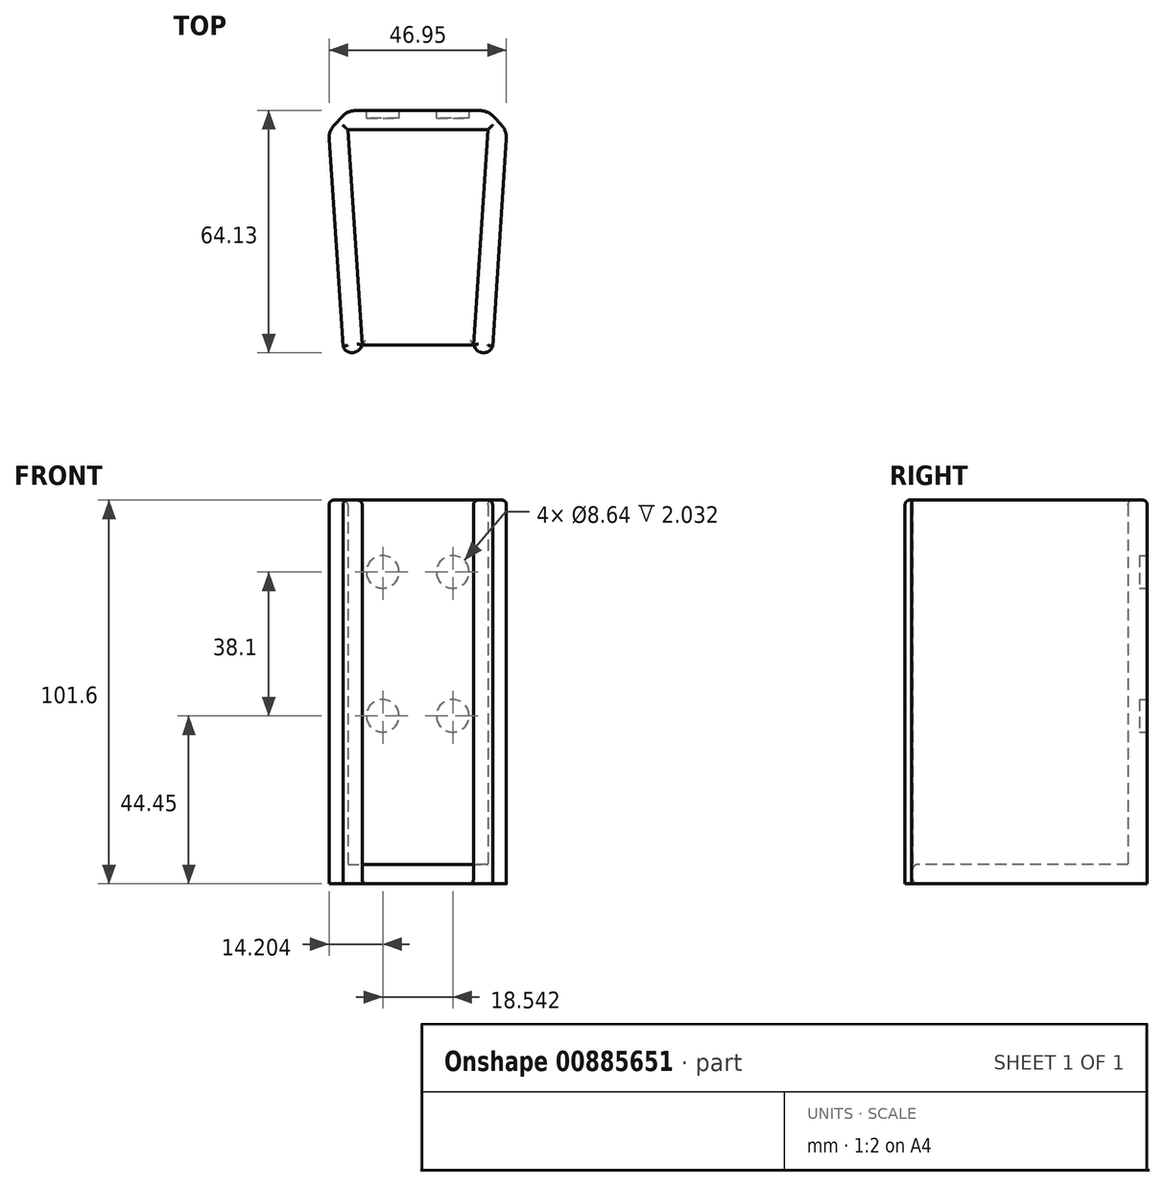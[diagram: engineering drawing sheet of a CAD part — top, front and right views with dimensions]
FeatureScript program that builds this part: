
annotation { "Feature Type Name" : "Feature", "Feature Type Description" : "" }
export const myFeature = defineFeature(function(context is Context, id is Id, definition is map)
    precondition{}
    {
        {
            var Q0;
            Q0=qCreatedBy(makeId("Top.planeOp"),FACE);
            var sketch = newSketch(context, id + "F0", { "sketchPlane" : qUnion([Q0])});
            skLineSegment(sketch, "E0", {"start": v(-16.69, 57.02) * mm, "end": v(20.4, 57.02) * mm});
            skLineSegment(sketch, "E1", {"start": v(-12.88, 0) * mm, "end": v(16.59, 0) * mm});
            skLineSegment(sketch, "E2", {"start": v(-16.69, 57.02) * mm, "end": v(-12.88, 0) * mm});
            skLineSegment(sketch, "E3", {"start": v(20.4, 57.02) * mm, "end": v(16.59, 0) * mm});
            skPoint(sketch, "E4", {"position": v(1.86, 57.02) * mm});
            skPoint(sketch, "E5", {"position": v(1.86, 0) * mm});
            skLineSegment(sketch, "E6.0", {"start": v(-16.69, 62.1) * mm, "end": v(20.4, 62.1) * mm});
            skLineSegment(sketch, "E7", {"start": v(20.4, 62.1) * mm, "end": v(20.4, 57.02) * mm});
            skLineSegment(sketch, "E8", {"start": v(-16.69, 62.1) * mm, "end": v(-16.69, 57.02) * mm});
            skLineSegment(sketch, "E9.0", {"start": v(-21.76, 56.68) * mm, "end": v(-17.95, -0.34) * mm});
            skLineSegment(sketch, "E10.0", {"start": v(25.47, 56.68) * mm, "end": v(21.66, -0.34) * mm});
            skLineSegment(sketch, "E11", {"start": v(-21.76, 56.68) * mm, "end": v(-16.69, 62.1) * mm});
            skLineSegment(sketch, "E12", {"start": v(20.4, 62.1) * mm, "end": v(25.47, 56.68) * mm});
            skLineSegment(sketch, "E13", {"start": v(21.66, -0.34) * mm, "end": v(20.4, -6.12) * mm});
            skLineSegment(sketch, "E14", {"start": v(16.59, 0) * mm, "end": v(20.4, -6.12) * mm});
            skLineSegment(sketch, "E15", {"start": v(1.86, 57.02) * mm, "end": v(1.86, 0) * mm, "construction": true});
            skLineSegment(sketch, "E16.MirrorCS", {"start": v(-12.88, 0) * mm, "end": v(-16.69, -6.12) * mm});
            skLineSegment(sketch, "E17.MirrorCS", {"start": v(-17.95, -0.34) * mm, "end": v(-16.69, -6.12) * mm});
            skSolve(sketch);
        }
        {
            var Q0;
            Q0=makeQuery(id+"F0.imprint","IMPRINT",FACE,{"disambiguationData":[TD([[makeQuery(id+"F0.imprint","IMPRINT",EDGE,{"derivedFrom":sQuery(id+"F0.wireOp",EDGE,"E2")}),-1.0]])]});
            var Q1;
            Q1=makeQuery(id+"F0.imprint","IMPRINT",FACE,{"disambiguationData":[TD([[makeQuery(id+"F0.imprint","IMPRINT",EDGE,{"derivedFrom":sQuery(id+"F0.wireOp",EDGE,"E0")}),1.0]])]});
            var Q2;
            Q2=makeQuery(id+"F0.imprint","IMPRINT",FACE,{"disambiguationData":[TD([[makeQuery(id+"F0.imprint","IMPRINT",EDGE,{"derivedFrom":sQuery(id+"F0.wireOp",EDGE,"E3")}),1.0]])]});
            extrude(context, id + "F1", {"entities" : qUnion([Q0, Q1, Q2]), "depth" : 96.52 * mm, "offsetDistance" : 25.4 * mm});
        }
        {
            var Q0;
            Q0=makeQuery(id+"F0.imprint","IMPRINT",FACE,{"disambiguationData":[TD([[makeQuery(id+"F0.imprint","IMPRINT",EDGE,{"derivedFrom":sQuery(id+"F0.wireOp",EDGE,"E0")}),-1.0]])]});
            var Q1;
            Q1=makeQuery(id+"F0.imprint","IMPRINT",FACE,{"disambiguationData":[TD([[makeQuery(id+"F0.imprint","IMPRINT",EDGE,{"derivedFrom":sQuery(id+"F0.wireOp",EDGE,"E3")}),1.0]])]});
            var Q2;
            Q2=makeQuery(id+"F0.imprint","IMPRINT",FACE,{"disambiguationData":[TD([[makeQuery(id+"F0.imprint","IMPRINT",EDGE,{"derivedFrom":sQuery(id+"F0.wireOp",EDGE,"E0")}),1.0]])]});
            var Q3;
            Q3=makeQuery(id+"F0.imprint","IMPRINT",FACE,{"disambiguationData":[TD([[makeQuery(id+"F0.imprint","IMPRINT",EDGE,{"derivedFrom":sQuery(id+"F0.wireOp",EDGE,"E2")}),-1.0]])]});
            extrude(context, id + "F2", {"entities" : qUnion([Q0, Q1, Q2, Q3]), "operationType" : NewBodyOperationType.ADD, "oppositeDirection" : true, "depth" : 5.08 * mm, "offsetDistance" : 25.4 * mm});
        }
        {
            var Q0;
            {var subQ0=sQuery(id+"F0.wireOp",EDGE,"E6.0");Q0=makeQuery(id+"F2.boolean.opBoolean","MERGE",FACE,{"derivedFrom":[makeQuery(id+"F1.opExtrude","SWEPT_FACE",FACE,{"disambiguationData":[OSD([subQ0])]}),makeQuery(id+"F2.opExtrude","SWEPT_FACE",FACE,{"disambiguationData":[OSD([subQ0])]})]});}
            var sketch = newSketch(context, id + "F3", { "sketchPlane" : qUnion([Q0])});
            skLineSegment(sketch, "E18", {"start": v(-1.86, 96.52) * mm, "end": v(-1.86, 0) * mm, "construction": true});
            skPoint(sketch, "E19", {"position": v(-1.86, 20.32) * mm});
            skPoint(sketch, "E20", {"position": v(-1.86, 77.47) * mm});
            skPoint(sketch, "E21", {"position": v(-1.86, 39.37) * mm});
            skPoint(sketch, "E22", {"position": v(-20.4, 39.37) * mm});
            skPoint(sketch, "E23", {"position": v(-20.4, 77.47) * mm});
            skPoint(sketch, "E24", {"position": v(16.69, 77.47) * mm});
            skPoint(sketch, "E25", {"position": v(16.69, 39.37) * mm});
            skLineSegment(sketch, "E26", {"start": v(-20.4, 77.47) * mm, "end": v(-1.86, 77.47) * mm, "construction": true});
            skLineSegment(sketch, "E27", {"start": v(-1.86, 77.47) * mm, "end": v(16.69, 77.47) * mm, "construction": true});
            skLineSegment(sketch, "E28", {"start": v(16.69, 39.37) * mm, "end": v(-1.86, 39.37) * mm, "construction": true});
            skLineSegment(sketch, "E29", {"start": v(-1.86, 39.37) * mm, "end": v(-20.4, 39.37) * mm, "construction": true});
            skCircle(sketch, "E30", {"center": v(-11.13, 77.47) * mm, "radius": 4.32 * mm});
            skCircle(sketch, "E31", {"center": v(7.42, 77.47) * mm, "radius": 4.32 * mm});
            skCircle(sketch, "E32", {"center": v(7.42, 39.37) * mm, "radius": 4.32 * mm});
            skCircle(sketch, "E33", {"center": v(-11.13, 39.37) * mm, "radius": 4.32 * mm});
            skSolve(sketch);
        }
        {
            var Q0;
            {var subQ0=sQuery(id+"F0.wireOp",EDGE,"E17.MirrorCS");var subQ1=sQuery(id+"F0.wireOp",EDGE,"E16.MirrorCS");Q0=makeQuery(id+"F2.boolean.opBoolean","MERGE",EDGE,{"derivedFrom":[makeQuery(id+"F1.opExtrude","SWEPT_EDGE",EDGE,{"disambiguationData":[OSD([subQ1,subQ0])]}),makeQuery(id+"F2.opExtrude","SWEPT_EDGE",EDGE,{"disambiguationData":[OSD([subQ1,subQ0])]})]});}
            var Q1;
            {var subQ0=sQuery(id+"F0.wireOp",EDGE,"E14");var subQ1=sQuery(id+"F0.wireOp",EDGE,"E13");Q1=makeQuery(id+"F2.boolean.opBoolean","MERGE",EDGE,{"derivedFrom":[makeQuery(id+"F1.opExtrude","SWEPT_EDGE",EDGE,{"disambiguationData":[OSD([subQ1,subQ0])]}),makeQuery(id+"F2.opExtrude","SWEPT_EDGE",EDGE,{"disambiguationData":[OSD([subQ1,subQ0])]})]});}
            fillet(context, id + "F4", {"entities" : qUnion([Q0, Q1]), "radius" : 2.54 * mm, "tangentPropagation" : true, "allowEdgeOverflow" : false});
        }
        {
            var Q0;
            {var subQ0=sQuery(id+"F0.wireOp",EDGE,"E11");var subQ1=sQuery(id+"F0.wireOp",EDGE,"E9.0");Q0=makeQuery(id+"F2.boolean.opBoolean","MERGE",EDGE,{"derivedFrom":[makeQuery(id+"F1.opExtrude","SWEPT_EDGE",EDGE,{"disambiguationData":[OSD([subQ1,subQ0])]}),makeQuery(id+"F2.opExtrude","SWEPT_EDGE",EDGE,{"disambiguationData":[OSD([subQ1,subQ0])]})]});}
            var Q1;
            {var subQ0=sQuery(id+"F0.wireOp",EDGE,"E11");var subQ1=sQuery(id+"F0.wireOp",EDGE,"E8");var subQ2=sQuery(id+"F0.wireOp",EDGE,"E6.0");Q1=makeQuery(id+"F2.boolean.opBoolean","MERGE",EDGE,{"derivedFrom":[makeQuery(id+"F1.opExtrude","SWEPT_EDGE",EDGE,{"disambiguationData":[OSD([subQ2,subQ1,subQ0])]}),makeQuery(id+"F2.opExtrude","SWEPT_EDGE",EDGE,{"disambiguationData":[OSD([subQ2,subQ1,subQ0])]})]});}
            var Q2;
            {var subQ0=sQuery(id+"F0.wireOp",EDGE,"E12");var subQ1=sQuery(id+"F0.wireOp",EDGE,"E7");var subQ2=sQuery(id+"F0.wireOp",EDGE,"E6.0");Q2=makeQuery(id+"F2.boolean.opBoolean","MERGE",EDGE,{"derivedFrom":[makeQuery(id+"F1.opExtrude","SWEPT_EDGE",EDGE,{"disambiguationData":[OSD([subQ2,subQ1,subQ0])]}),makeQuery(id+"F2.opExtrude","SWEPT_EDGE",EDGE,{"disambiguationData":[OSD([subQ2,subQ1,subQ0])]})]});}
            var Q3;
            {var subQ0=sQuery(id+"F0.wireOp",EDGE,"E12");var subQ1=sQuery(id+"F0.wireOp",EDGE,"E10.0");Q3=makeQuery(id+"F2.boolean.opBoolean","MERGE",EDGE,{"derivedFrom":[makeQuery(id+"F1.opExtrude","SWEPT_EDGE",EDGE,{"disambiguationData":[OSD([subQ1,subQ0])]}),makeQuery(id+"F2.opExtrude","SWEPT_EDGE",EDGE,{"disambiguationData":[OSD([subQ1,subQ0])]})]});}
            fillet(context, id + "F5", {"entities" : qUnion([Q0, Q1, Q2, Q3]), "radius" : 5.08 * mm, "tangentPropagation" : true, "allowEdgeOverflow" : false});
        }
        {
            var Q0;
            Q0=makeQuery(id+"F3.imprint","IMPRINT",FACE,{"disambiguationData":[TD([[makeQuery(id+"F3.imprint","IMPRINT",EDGE,{"derivedFrom":sQuery(id+"F3.wireOp",EDGE,"E30")}),1.0]])]});
            var Q1;
            Q1=makeQuery(id+"F3.imprint","IMPRINT",FACE,{"disambiguationData":[TD([[makeQuery(id+"F3.imprint","IMPRINT",EDGE,{"derivedFrom":sQuery(id+"F3.wireOp",EDGE,"E31")}),1.0]])]});
            var Q2;
            Q2=makeQuery(id+"F3.imprint","IMPRINT",FACE,{"disambiguationData":[TD([[makeQuery(id+"F3.imprint","IMPRINT",EDGE,{"derivedFrom":sQuery(id+"F3.wireOp",EDGE,"E32")}),1.0]])]});
            var Q3;
            Q3=makeQuery(id+"F3.imprint","IMPRINT",FACE,{"disambiguationData":[TD([[makeQuery(id+"F3.imprint","IMPRINT",EDGE,{"derivedFrom":sQuery(id+"F3.wireOp",EDGE,"E33")}),1.0]])]});
            extrude(context, id + "F6", {"entities" : qUnion([Q0, Q1, Q2, Q3]), "operationType" : NewBodyOperationType.REMOVE, "oppositeDirection" : true, "depth" : 2.03 * mm, "offsetDistance" : 25.4 * mm});
        }
        {
            var Q0;
            Q0=makeQuery(id+"F1.opExtrude","CAP_EDGE",EDGE,{"disambiguationData":[OSD([sQuery(id+"F0.wireOp",EDGE,"E0")])],"isStart":true});
            var Q1;
            Q1=makeQuery(id+"F1.opExtrude","CAP_EDGE",EDGE,{"disambiguationData":[OSD([sQuery(id+"F0.wireOp",EDGE,"E3")])],"isStart":true});
            var Q2;
            Q2=makeQuery(id+"F1.opExtrude","CAP_EDGE",EDGE,{"disambiguationData":[OSD([sQuery(id+"F0.wireOp",EDGE,"E2")])],"isStart":true});
            var Q3;
            Q3=makeQuery(id+"F1.opExtrude","CAP_EDGE",EDGE,{"disambiguationData":[OSD([sQuery(id+"F0.wireOp",EDGE,"E2")])],"isStart":false});
            var Q4;
            Q4=makeQuery(id+"F1.opExtrude","CAP_EDGE",EDGE,{"disambiguationData":[OSD([sQuery(id+"F0.wireOp",EDGE,"E3")])],"isStart":false});
            var Q5;
            Q5=makeQuery(id+"F1.opExtrude","CAP_EDGE",EDGE,{"disambiguationData":[OSD([sQuery(id+"F0.wireOp",EDGE,"E10.0")])],"isStart":false});
            var Q6;
            Q6=makeQuery(id+"F1.opExtrude","CAP_EDGE",EDGE,{"disambiguationData":[OSD([sQuery(id+"F0.wireOp",EDGE,"E9.0")])],"isStart":false});
            var Q7;
            Q7=makeQuery(id+"F1.opExtrude","CAP_EDGE",EDGE,{"disambiguationData":[OSD([sQuery(id+"F0.wireOp",EDGE,"E6.0")])],"isStart":false});
            var Q8;
            Q8=makeQuery(id+"F1.opExtrude","CAP_EDGE",EDGE,{"disambiguationData":[OSD([sQuery(id+"F0.wireOp",EDGE,"E12")])],"isStart":false});
            var Q9;
            {var subQ0=sQuery(id+"F0.wireOp",EDGE,"E12");var subQ1=sQuery(id+"F0.wireOp",EDGE,"E6.0");var subQ2=sQuery(id+"F0.wireOp",EDGE,"E7");Q9=makeQuery(id+"F5.opFillet","BLEND_EDGE",EDGE,{"blendedFrom":[makeQuery(id+"F2.boolean.opBoolean","MERGE",EDGE,{"derivedFrom":[makeQuery(id+"F1.opExtrude","SWEPT_EDGE",EDGE,{"disambiguationData":[OSD([subQ1,subQ2,subQ0])]}),makeQuery(id+"F2.opExtrude","SWEPT_EDGE",EDGE,{"disambiguationData":[OSD([subQ1,subQ2,subQ0])]})]}),makeQuery(id+"F1.opExtrude","CAP_FACE",FACE,{"disambiguationData":[OSD([sQuery(id+"F0.wireOp",EDGE,"E0"),sQuery(id+"F0.wireOp",EDGE,"E2"),sQuery(id+"F0.wireOp",EDGE,"E3"),subQ1,sQuery(id+"F0.wireOp",EDGE,"E9.0"),sQuery(id+"F0.wireOp",EDGE,"E10.0"),sQuery(id+"F0.wireOp",EDGE,"E11"),subQ0,sQuery(id+"F0.wireOp",EDGE,"E13"),sQuery(id+"F0.wireOp",EDGE,"E14"),sQuery(id+"F0.wireOp",EDGE,"E16.MirrorCS"),sQuery(id+"F0.wireOp",EDGE,"E17.MirrorCS")])],"isStart":false})],"blendedInto":[makeQuery(id+"F1.opExtrude","CAP_FACE",FACE,{"disambiguationData":[OSD([sQuery(id+"F0.wireOp",EDGE,"E0"),sQuery(id+"F0.wireOp",EDGE,"E2"),sQuery(id+"F0.wireOp",EDGE,"E3"),subQ1,sQuery(id+"F0.wireOp",EDGE,"E9.0"),sQuery(id+"F0.wireOp",EDGE,"E10.0"),sQuery(id+"F0.wireOp",EDGE,"E11"),subQ0,sQuery(id+"F0.wireOp",EDGE,"E13"),sQuery(id+"F0.wireOp",EDGE,"E14"),sQuery(id+"F0.wireOp",EDGE,"E16.MirrorCS"),sQuery(id+"F0.wireOp",EDGE,"E17.MirrorCS")])],"isStart":false})]});}
            var Q10;
            {var subQ0=sQuery(id+"F0.wireOp",EDGE,"E12");var subQ1=sQuery(id+"F0.wireOp",EDGE,"E10.0");Q10=makeQuery(id+"F5.opFillet","BLEND_EDGE",EDGE,{"blendedFrom":[makeQuery(id+"F2.boolean.opBoolean","MERGE",EDGE,{"derivedFrom":[makeQuery(id+"F1.opExtrude","SWEPT_EDGE",EDGE,{"disambiguationData":[OSD([subQ1,subQ0])]}),makeQuery(id+"F2.opExtrude","SWEPT_EDGE",EDGE,{"disambiguationData":[OSD([subQ1,subQ0])]})]}),makeQuery(id+"F1.opExtrude","CAP_FACE",FACE,{"disambiguationData":[OSD([sQuery(id+"F0.wireOp",EDGE,"E0"),sQuery(id+"F0.wireOp",EDGE,"E2"),sQuery(id+"F0.wireOp",EDGE,"E3"),sQuery(id+"F0.wireOp",EDGE,"E6.0"),sQuery(id+"F0.wireOp",EDGE,"E9.0"),subQ1,sQuery(id+"F0.wireOp",EDGE,"E11"),subQ0,sQuery(id+"F0.wireOp",EDGE,"E13"),sQuery(id+"F0.wireOp",EDGE,"E14"),sQuery(id+"F0.wireOp",EDGE,"E16.MirrorCS"),sQuery(id+"F0.wireOp",EDGE,"E17.MirrorCS")])],"isStart":false})],"blendedInto":[makeQuery(id+"F1.opExtrude","CAP_FACE",FACE,{"disambiguationData":[OSD([sQuery(id+"F0.wireOp",EDGE,"E0"),sQuery(id+"F0.wireOp",EDGE,"E2"),sQuery(id+"F0.wireOp",EDGE,"E3"),sQuery(id+"F0.wireOp",EDGE,"E6.0"),sQuery(id+"F0.wireOp",EDGE,"E9.0"),subQ1,sQuery(id+"F0.wireOp",EDGE,"E11"),subQ0,sQuery(id+"F0.wireOp",EDGE,"E13"),sQuery(id+"F0.wireOp",EDGE,"E14"),sQuery(id+"F0.wireOp",EDGE,"E16.MirrorCS"),sQuery(id+"F0.wireOp",EDGE,"E17.MirrorCS")])],"isStart":false})]});}
            var Q11;
            {var subQ0=sQuery(id+"F0.wireOp",EDGE,"E11");var subQ1=sQuery(id+"F0.wireOp",EDGE,"E6.0");var subQ2=sQuery(id+"F0.wireOp",EDGE,"E8");Q11=makeQuery(id+"F5.opFillet","BLEND_EDGE",EDGE,{"blendedFrom":[makeQuery(id+"F2.boolean.opBoolean","MERGE",EDGE,{"derivedFrom":[makeQuery(id+"F1.opExtrude","SWEPT_EDGE",EDGE,{"disambiguationData":[OSD([subQ1,subQ2,subQ0])]}),makeQuery(id+"F2.opExtrude","SWEPT_EDGE",EDGE,{"disambiguationData":[OSD([subQ1,subQ2,subQ0])]})]}),makeQuery(id+"F1.opExtrude","CAP_FACE",FACE,{"disambiguationData":[OSD([sQuery(id+"F0.wireOp",EDGE,"E0"),sQuery(id+"F0.wireOp",EDGE,"E2"),sQuery(id+"F0.wireOp",EDGE,"E3"),subQ1,sQuery(id+"F0.wireOp",EDGE,"E9.0"),sQuery(id+"F0.wireOp",EDGE,"E10.0"),subQ0,sQuery(id+"F0.wireOp",EDGE,"E12"),sQuery(id+"F0.wireOp",EDGE,"E13"),sQuery(id+"F0.wireOp",EDGE,"E14"),sQuery(id+"F0.wireOp",EDGE,"E16.MirrorCS"),sQuery(id+"F0.wireOp",EDGE,"E17.MirrorCS")])],"isStart":false})],"blendedInto":[makeQuery(id+"F1.opExtrude","CAP_FACE",FACE,{"disambiguationData":[OSD([sQuery(id+"F0.wireOp",EDGE,"E0"),sQuery(id+"F0.wireOp",EDGE,"E2"),sQuery(id+"F0.wireOp",EDGE,"E3"),subQ1,sQuery(id+"F0.wireOp",EDGE,"E9.0"),sQuery(id+"F0.wireOp",EDGE,"E10.0"),subQ0,sQuery(id+"F0.wireOp",EDGE,"E12"),sQuery(id+"F0.wireOp",EDGE,"E13"),sQuery(id+"F0.wireOp",EDGE,"E14"),sQuery(id+"F0.wireOp",EDGE,"E16.MirrorCS"),sQuery(id+"F0.wireOp",EDGE,"E17.MirrorCS")])],"isStart":false})]});}
            var Q12;
            Q12=makeQuery(id+"F1.opExtrude","CAP_EDGE",EDGE,{"disambiguationData":[OSD([sQuery(id+"F0.wireOp",EDGE,"E11")])],"isStart":false});
            var Q13;
            {var subQ0=sQuery(id+"F0.wireOp",EDGE,"E11");var subQ1=sQuery(id+"F0.wireOp",EDGE,"E9.0");Q13=makeQuery(id+"F5.opFillet","BLEND_EDGE",EDGE,{"blendedFrom":[makeQuery(id+"F2.boolean.opBoolean","MERGE",EDGE,{"derivedFrom":[makeQuery(id+"F1.opExtrude","SWEPT_EDGE",EDGE,{"disambiguationData":[OSD([subQ1,subQ0])]}),makeQuery(id+"F2.opExtrude","SWEPT_EDGE",EDGE,{"disambiguationData":[OSD([subQ1,subQ0])]})]}),makeQuery(id+"F1.opExtrude","CAP_FACE",FACE,{"disambiguationData":[OSD([sQuery(id+"F0.wireOp",EDGE,"E0"),sQuery(id+"F0.wireOp",EDGE,"E2"),sQuery(id+"F0.wireOp",EDGE,"E3"),sQuery(id+"F0.wireOp",EDGE,"E6.0"),subQ1,sQuery(id+"F0.wireOp",EDGE,"E10.0"),subQ0,sQuery(id+"F0.wireOp",EDGE,"E12"),sQuery(id+"F0.wireOp",EDGE,"E13"),sQuery(id+"F0.wireOp",EDGE,"E14"),sQuery(id+"F0.wireOp",EDGE,"E16.MirrorCS"),sQuery(id+"F0.wireOp",EDGE,"E17.MirrorCS")])],"isStart":false})],"blendedInto":[makeQuery(id+"F1.opExtrude","CAP_FACE",FACE,{"disambiguationData":[OSD([sQuery(id+"F0.wireOp",EDGE,"E0"),sQuery(id+"F0.wireOp",EDGE,"E2"),sQuery(id+"F0.wireOp",EDGE,"E3"),sQuery(id+"F0.wireOp",EDGE,"E6.0"),subQ1,sQuery(id+"F0.wireOp",EDGE,"E10.0"),subQ0,sQuery(id+"F0.wireOp",EDGE,"E12"),sQuery(id+"F0.wireOp",EDGE,"E13"),sQuery(id+"F0.wireOp",EDGE,"E14"),sQuery(id+"F0.wireOp",EDGE,"E16.MirrorCS"),sQuery(id+"F0.wireOp",EDGE,"E17.MirrorCS")])],"isStart":false})]});}
            var Q14;
            Q14=makeQuery(id+"F1.opExtrude","CAP_EDGE",EDGE,{"disambiguationData":[OSD([sQuery(id+"F0.wireOp",EDGE,"E0")])],"isStart":false});
            var Q15;
            {var subQ0=sQuery(id+"F0.wireOp",EDGE,"E14");var subQ1=sQuery(id+"F0.wireOp",EDGE,"E13");Q15=makeQuery(id+"F4.opFillet","BLEND_EDGE",EDGE,{"blendedFrom":[makeQuery(id+"F2.boolean.opBoolean","MERGE",EDGE,{"derivedFrom":[makeQuery(id+"F1.opExtrude","SWEPT_EDGE",EDGE,{"disambiguationData":[OSD([subQ1,subQ0])]}),makeQuery(id+"F2.opExtrude","SWEPT_EDGE",EDGE,{"disambiguationData":[OSD([subQ1,subQ0])]})]}),makeQuery(id+"F1.opExtrude","CAP_FACE",FACE,{"disambiguationData":[OSD([sQuery(id+"F0.wireOp",EDGE,"E0"),sQuery(id+"F0.wireOp",EDGE,"E2"),sQuery(id+"F0.wireOp",EDGE,"E3"),sQuery(id+"F0.wireOp",EDGE,"E6.0"),sQuery(id+"F0.wireOp",EDGE,"E9.0"),sQuery(id+"F0.wireOp",EDGE,"E10.0"),sQuery(id+"F0.wireOp",EDGE,"E11"),sQuery(id+"F0.wireOp",EDGE,"E12"),subQ1,subQ0,sQuery(id+"F0.wireOp",EDGE,"E16.MirrorCS"),sQuery(id+"F0.wireOp",EDGE,"E17.MirrorCS")])],"isStart":false})],"blendedInto":[makeQuery(id+"F1.opExtrude","CAP_FACE",FACE,{"disambiguationData":[OSD([sQuery(id+"F0.wireOp",EDGE,"E0"),sQuery(id+"F0.wireOp",EDGE,"E2"),sQuery(id+"F0.wireOp",EDGE,"E3"),sQuery(id+"F0.wireOp",EDGE,"E6.0"),sQuery(id+"F0.wireOp",EDGE,"E9.0"),sQuery(id+"F0.wireOp",EDGE,"E10.0"),sQuery(id+"F0.wireOp",EDGE,"E11"),sQuery(id+"F0.wireOp",EDGE,"E12"),subQ1,subQ0,sQuery(id+"F0.wireOp",EDGE,"E16.MirrorCS"),sQuery(id+"F0.wireOp",EDGE,"E17.MirrorCS")])],"isStart":false})]});}
            var Q16;
            {var subQ0=sQuery(id+"F0.wireOp",EDGE,"E17.MirrorCS");var subQ1=sQuery(id+"F0.wireOp",EDGE,"E16.MirrorCS");Q16=makeQuery(id+"F4.opFillet","BLEND_EDGE",EDGE,{"blendedFrom":[makeQuery(id+"F2.boolean.opBoolean","MERGE",EDGE,{"derivedFrom":[makeQuery(id+"F1.opExtrude","SWEPT_EDGE",EDGE,{"disambiguationData":[OSD([subQ1,subQ0])]}),makeQuery(id+"F2.opExtrude","SWEPT_EDGE",EDGE,{"disambiguationData":[OSD([subQ1,subQ0])]})]}),makeQuery(id+"F1.opExtrude","CAP_FACE",FACE,{"disambiguationData":[OSD([sQuery(id+"F0.wireOp",EDGE,"E0"),sQuery(id+"F0.wireOp",EDGE,"E2"),sQuery(id+"F0.wireOp",EDGE,"E3"),sQuery(id+"F0.wireOp",EDGE,"E6.0"),sQuery(id+"F0.wireOp",EDGE,"E9.0"),sQuery(id+"F0.wireOp",EDGE,"E10.0"),sQuery(id+"F0.wireOp",EDGE,"E11"),sQuery(id+"F0.wireOp",EDGE,"E12"),sQuery(id+"F0.wireOp",EDGE,"E13"),sQuery(id+"F0.wireOp",EDGE,"E14"),subQ1,subQ0])],"isStart":false})],"blendedInto":[makeQuery(id+"F1.opExtrude","CAP_FACE",FACE,{"disambiguationData":[OSD([sQuery(id+"F0.wireOp",EDGE,"E0"),sQuery(id+"F0.wireOp",EDGE,"E2"),sQuery(id+"F0.wireOp",EDGE,"E3"),sQuery(id+"F0.wireOp",EDGE,"E6.0"),sQuery(id+"F0.wireOp",EDGE,"E9.0"),sQuery(id+"F0.wireOp",EDGE,"E10.0"),sQuery(id+"F0.wireOp",EDGE,"E11"),sQuery(id+"F0.wireOp",EDGE,"E12"),sQuery(id+"F0.wireOp",EDGE,"E13"),sQuery(id+"F0.wireOp",EDGE,"E14"),subQ1,subQ0])],"isStart":false})]});}
            var Q17;
            Q17=makeQuery(id+"F2.opExtrude","CAP_EDGE",EDGE,{"disambiguationData":[OSD([sQuery(id+"F0.wireOp",EDGE,"E1")])],"isStart":false});
            fillet(context, id + "F7", {"entities" : qUnion([Q0, Q1, Q2, Q3, Q4, Q5, Q6, Q7, Q8, Q9, Q10, Q11, Q12, Q13, Q14, Q15, Q16, Q17]), "radius" : 1.27 * mm, "tangentPropagation" : true, "allowEdgeOverflow" : false});
        }
        {
            var Q0;
            Q0=makeQuery(id+"F2.opExtrude","CAP_EDGE",EDGE,{"disambiguationData":[OSD([sQuery(id+"F0.wireOp",EDGE,"E1")])],"isStart":true});
            fillet(context, id + "F8", {"entities" : qUnion([Q0]), "radius" : 1.27 * mm, "tangentPropagation" : true, "allowEdgeOverflow" : false});
        }
    });
